FCSTD DOCUMENT  (FreeCAD 0.18R4 (GitTag))
Label: x2_filas_8_dupont
License: All rights reserved
LicenseURL: http://en.wikipedia.org/wiki/All_rights_reserved
objects: Sketcher::SketchObject×1, PartDesign::Body×1, Spreadsheet::Sheet×1
note: 2 computed .brp shape members not serialized (recipe doc carries the construction recipe); baked Part::Feature solids carry a one-line shape summary decoded from their .brp

FEATURE [Sketcher::SketchObject] Sketch
  MapMode = 5
  Placement = pos=(0,0,0) rot=(1,0,0;1.5708rad)
  Support = -> [XZ_Plane]
  expr: Constraints[24] = param.exteinde_base
  expr: Constraints[11] = param.alto_fichas
  expr: Constraints[1] = param.mitad_base
  sketch-geometry (11):
    g0: LineSegment StartX=-15.3 StartY=0 StartZ=0 EndX=0 EndY=0 EndZ=0
    g1: ArcOfCircle CenterX=-15.3 CenterY=2.5 CenterZ=0 NormalX=0 NormalY=0 NormalZ=1 AngleXU=0 Radius=2.5 StartAngle=3.14159 EndAngle=4.71239
    g2: LineSegment StartX=-17.8 StartY=2.5 StartZ=0 EndX=-20.8 EndY=2.5 EndZ=0
    g3: ArcOfCircle CenterX=-20.8 CenterY=7.9 CenterZ=0 NormalX=0 NormalY=0 NormalZ=1 AngleXU=0 Radius=5.4 StartAngle=1.5708 EndAngle=4.71239
    g4: LineSegment StartX=-20.8 StartY=13.3 StartZ=0 EndX=-17.8 EndY=13.3 EndZ=0
    g5: LineSegment StartX=-17.8 StartY=13.3 StartZ=0 EndX=-17.8 EndY=15.1 EndZ=0
    g6: ArcOfCircle CenterX=-15.3 CenterY=15.1 CenterZ=0 NormalX=0 NormalY=0 NormalZ=1 AngleXU=0 Radius=2.5 StartAngle=1.5708 EndAngle=3.14159
    g7: LineSegment StartX=-15.3 StartY=17.6 StartZ=0 EndX=-13.8 EndY=17.6 EndZ=0
    g8: LineSegment StartX=-13.8 StartY=17.6 StartZ=0 EndX=-13.8 EndY=13.3 EndZ=0
    g9: LineSegment StartX=-13.8 StartY=13.3 StartZ=0 EndX=0 EndY=13.3 EndZ=0
    g10: LineSegment StartX=0 StartY=13.3 StartZ=0 EndX=0 EndY=0 EndZ=0
  constraints (33):
    c: Horizontal(g0)
    c: DistanceX(g0,g0) = 15.3
    c: Radius(g1) = 2.5
    c: DistanceX(g2,g2) = 3
    c: Horizontal(g1,g1)
    c: Coincident(g0,g-1)
    c: Tangent(g1,g0,g1) = -1.5708
    c: Coincident(g1,g0)
    c: Coincident(g2,g1)
    c: Horizontal(g2)
    c: Tangent(g3,g2) = 1.5708
    c: Diameter(g3) = 10.8
    c: Coincident(g4,g3)
    c: Horizontal(g4)
    c: Equal(g2,g4)
    c: Coincident(g5,g4)
    c: Vertical(g5)
    c: DistanceY(g5,g5) = 1.8
    c: Equal(g1,g6)
    c: Vertical(g6,g1)
    c: Tangent(g6,g5) = 1.5708
    c: Vertical(g6,g6)
    c: Coincident(g7,g6)
    c: Horizontal(g7)
    c: DistanceX(g7,g7) = 1.5
    c: Coincident(g8,g7)
    c: Vertical(g8)
    c: Horizontal(g8,g4)
    c: Coincident(g9,g8)
    c: Horizontal(g9)
    c: PointOnObject(g9,g-2)
    c: Coincident(g10,g9)
    c: Coincident(g10,g0)
FEATURE [PartDesign::Body] Body
  Group = -> [Sketch]
  Origin = -> Origin
FEATURE [Spreadsheet::Sheet] Spreadsheet  label="param"
  cells = A2=filas; B2(filas)=6; A3=huecos; B3(huecos)==filas - 1; A5=espacio ficha; B5(ficha)=2.7; A6=separa cable; B6(separa_cable)=0.5; A7=espacio cable; B7(cable)==ficha - 2 * separa_cable; A8=espacio separador; B8(separador)=1; A9=medio separador; B9(medio_Separador)==separador / 2; A11=ancho_fichas; B11(ancho_fichas)==filas * ficha; A12=ancho_separadores; B12(ancho_separadores)==huecos * separador; A13=ancho fichas menos; B13(ancho_fichas_menos)==ancho_fichas + ancho_separadores - 2 * medio_Separador; A15=mitad_base_ancho_fichas; B15(mitad_base_fichas)==ancho_fichas_menos / 2; A16=extiende_base; B16(exteinde_base)=1.5; A18=mitad_base; B18(mitad_base)==mitad_base_fichas + exteinde_base; A19=alto_fichas; B19(alto_fichas)==4 * ficha
